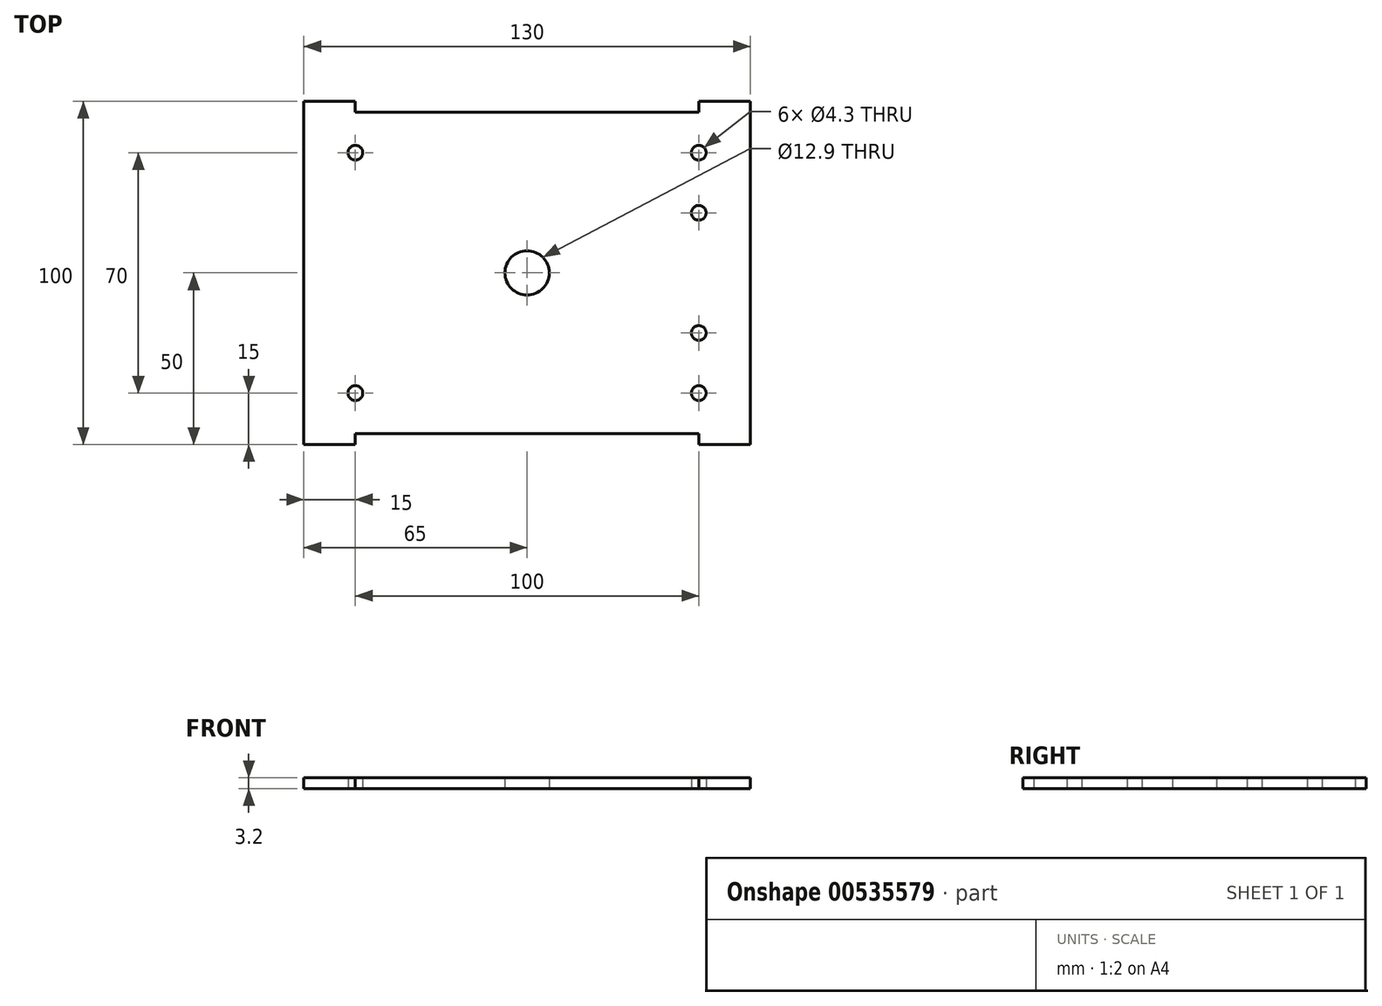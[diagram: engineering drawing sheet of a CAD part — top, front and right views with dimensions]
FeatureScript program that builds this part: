
annotation { "Feature Type Name" : "Feature", "Feature Type Description" : "" }
export const myFeature = defineFeature(function(context is Context, id is Id, definition is map)
    precondition{}
    {
        {
            var Q0;
            Q0=qCreatedBy(makeId("Top.planeOp"),FACE);
            var sketch = newSketch(context, id + "F0", { "sketchPlane" : qUnion([Q0])});
            skLineSegment(sketch, "E0.bottom", {"start": v(-65, 50) * mm, "end": v(65, 50) * mm});
            skLineSegment(sketch, "E0.top", {"start": v(-65, -50) * mm, "end": v(65, -50) * mm});
            skLineSegment(sketch, "E0.left", {"start": v(-65, 50) * mm, "end": v(-65, -50) * mm});
            skLineSegment(sketch, "E0.right", {"start": v(65, 50) * mm, "end": v(65, -50) * mm});
            skPoint(sketch, "E0.middle", {"position": v(0, 0) * mm});
            skSolve(sketch);
        }
        {
            var Q0;
            Q0=qSketchRegion(id+"F0",true);
            extrude(context, id + "F1", {"entities" : qUnion([Q0]), "depth" : 3.2 * mm, "offsetDistance" : 25 * mm});
        }
        {
            var Q0;
            Q0=qCreatedBy(makeId("Top.planeOp"),FACE);
            var sketch = newSketch(context, id + "F2", { "sketchPlane" : qUnion([Q0])});
            skCircle(sketch, "E1", {"center": v(-50, 35) * mm, "radius": 2.15 * mm});
            skCircle(sketch, "E2", {"center": v(50, 35) * mm, "radius": 2.15 * mm});
            skCircle(sketch, "E3", {"center": v(50, -35) * mm, "radius": 2.15 * mm});
            skCircle(sketch, "E4", {"center": v(-50, -35) * mm, "radius": 2.15 * mm});
            skCircle(sketch, "E5", {"center": v(50, 17.5) * mm, "radius": 2.15 * mm});
            skCircle(sketch, "E6.MirrorC", {"center": v(50, -17.5) * mm, "radius": 2.15 * mm});
            skLineSegment(sketch, "E7.bottom", {"start": v(-50, 50) * mm, "end": v(50, 50) * mm});
            skLineSegment(sketch, "E7.top", {"start": v(-50, 46.8) * mm, "end": v(50, 46.8) * mm});
            skLineSegment(sketch, "E7.left", {"start": v(-50, 50) * mm, "end": v(-50, 46.8) * mm});
            skLineSegment(sketch, "E7.right", {"start": v(50, 50) * mm, "end": v(50, 46.8) * mm});
            skLineSegment(sketch, "E8.MirrorCS", {"start": v(-50, -46.8) * mm, "end": v(50, -46.8) * mm});
            skLineSegment(sketch, "E9.MirrorCS", {"start": v(50, -50) * mm, "end": v(50, -46.8) * mm});
            skLineSegment(sketch, "E10.MirrorCS", {"start": v(-50, -50) * mm, "end": v(50, -50) * mm});
            skLineSegment(sketch, "E11.MirrorCS", {"start": v(-50, -50) * mm, "end": v(-50, -46.8) * mm});
            skCircle(sketch, "E12", {"center": v(0, 0) * mm, "radius": 6.45 * mm});
            skSolve(sketch);
        }
        {
            var Q0;
            Q0=qSketchRegion(id+"F2",true);
            extrude(context, id + "F3", {"entities" : qUnion([Q0]), "operationType" : NewBodyOperationType.REMOVE, "depth" : 40 * mm});
        }
    });
